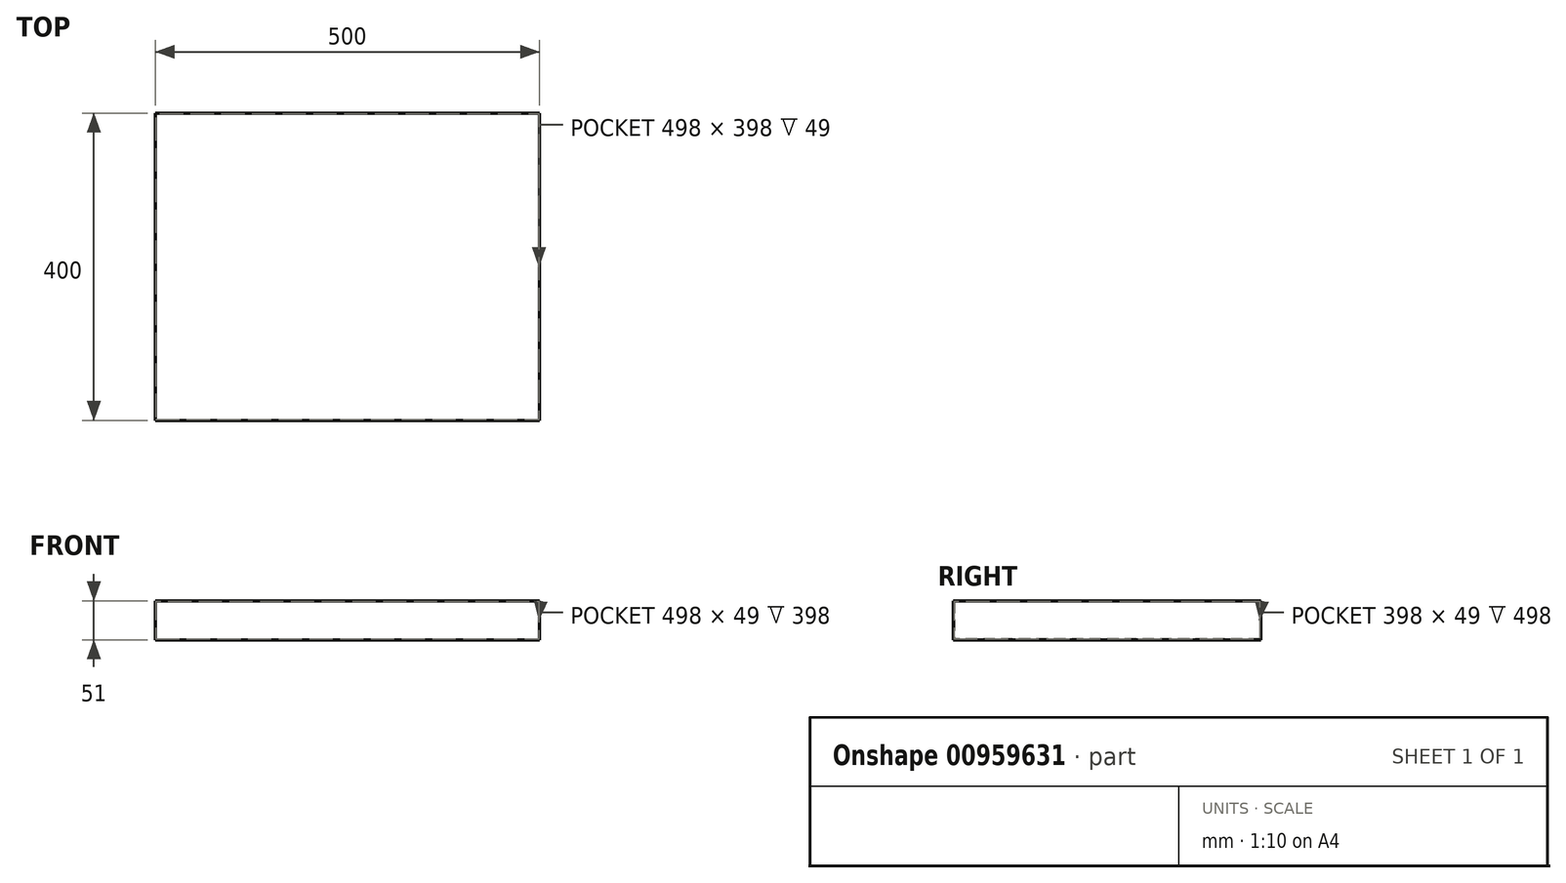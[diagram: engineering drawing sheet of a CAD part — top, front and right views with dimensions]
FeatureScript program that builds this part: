
annotation { "Feature Type Name" : "Feature", "Feature Type Description" : "" }
export const myFeature = defineFeature(function(context is Context, id is Id, definition is map)
    precondition{}
    {
        {
            var Q0;
            Q0=qCreatedBy(makeId("Top.planeOp"),FACE);
            var sketch = newSketch(context, id + "F0", { "sketchPlane" : qUnion([Q0])});
            skLineSegment(sketch, "E0.bottom", {"start": v(-250, 200) * mm, "end": v(250, 200) * mm});
            skLineSegment(sketch, "E0.top", {"start": v(-250, -200) * mm, "end": v(250, -200) * mm});
            skLineSegment(sketch, "E0.left", {"start": v(-250, 200) * mm, "end": v(-250, -200) * mm});
            skLineSegment(sketch, "E0.right", {"start": v(250, 200) * mm, "end": v(250, -200) * mm});
            skPoint(sketch, "E0.middle", {"position": v(0, 0) * mm});
            skSolve(sketch);
        }
        {
            var Q0;
            Q0 = qSketchRegion(id + "F0", true);
            extrude(context, id + "F1", {"entities" : qUnion([Q0]), "depth" : 50 * mm, "offsetDistance" : 25 * mm});
        }
        {
            var Q0;
            Q0=makeQuery(id+"F1.opExtrude","CAP_FACE",FACE,{"disambiguationData":[OSD([sQuery(id+"F0.wireOp",EDGE,"E0.bottom"),sQuery(id+"F0.wireOp",EDGE,"E0.top"),sQuery(id+"F0.wireOp",EDGE,"E0.left"),sQuery(id+"F0.wireOp",EDGE,"E0.right")])],"isStart":false});
            shell(context, id + "F2", {"entities" : qUnion([Q0]), "thickness" : 1 * mm});
        }
        {
            var Q0;
            Q0=makeQuery(id+"F1.opExtrude","CAP_FACE",FACE,{"disambiguationData":[OSD([sQuery(id+"F0.wireOp",EDGE,"E0.bottom"),sQuery(id+"F0.wireOp",EDGE,"E0.top"),sQuery(id+"F0.wireOp",EDGE,"E0.left"),sQuery(id+"F0.wireOp",EDGE,"E0.right")])],"isStart":false});
            cPlane(context, id + "F3", {"entities" : qUnion([Q0]), "cplaneType" : CPlaneType.OFFSET, "offset" : 0 * mm, "width" : 150 * mm, "height" : 150 * mm});
        }
        {
            var Q0;
            Q0=qCreatedBy(id+"F3.planeOp",FACE);
            var sketch = newSketch(context, id + "F4", { "sketchPlane" : qUnion([Q0])});
            skLineSegment(sketch, "E1.bottom", {"start": v(-250, -200) * mm, "end": v(250, -200) * mm});
            skLineSegment(sketch, "E1.top", {"start": v(-250, 200) * mm, "end": v(250, 200) * mm});
            skLineSegment(sketch, "E1.left", {"start": v(-250, -200) * mm, "end": v(-250, 200) * mm});
            skLineSegment(sketch, "E1.right", {"start": v(250, -200) * mm, "end": v(250, 200) * mm});
            skPoint(sketch, "E1.middle", {"position": v(0, 0) * mm});
            skSolve(sketch);
        }
        {
            var Q0;
            Q0 = qSketchRegion(id + "F4", true);
            extrude(context, id + "F5", {"entities" : qUnion([Q0]), "operationType" : NewBodyOperationType.ADD, "depth" : 1 * mm, "offsetDistance" : 25 * mm});
        }
        {
            var Q0;
            Q0=makeQuery(id+"F5.opExtrude","CAP_FACE",FACE,{"disambiguationData":[OSD([sQuery(id+"F4.wireOp",EDGE,"E1.bottom"),sQuery(id+"F4.wireOp",EDGE,"E1.top"),sQuery(id+"F4.wireOp",EDGE,"E1.left"),sQuery(id+"F4.wireOp",EDGE,"E1.right")])],"isStart":false});
            cPlane(context, id + "F6", {"entities" : qUnion([Q0]), "cplaneType" : CPlaneType.OFFSET, "offset" : 0 * mm, "width" : 150 * mm, "height" : 150 * mm});
        }
    });
